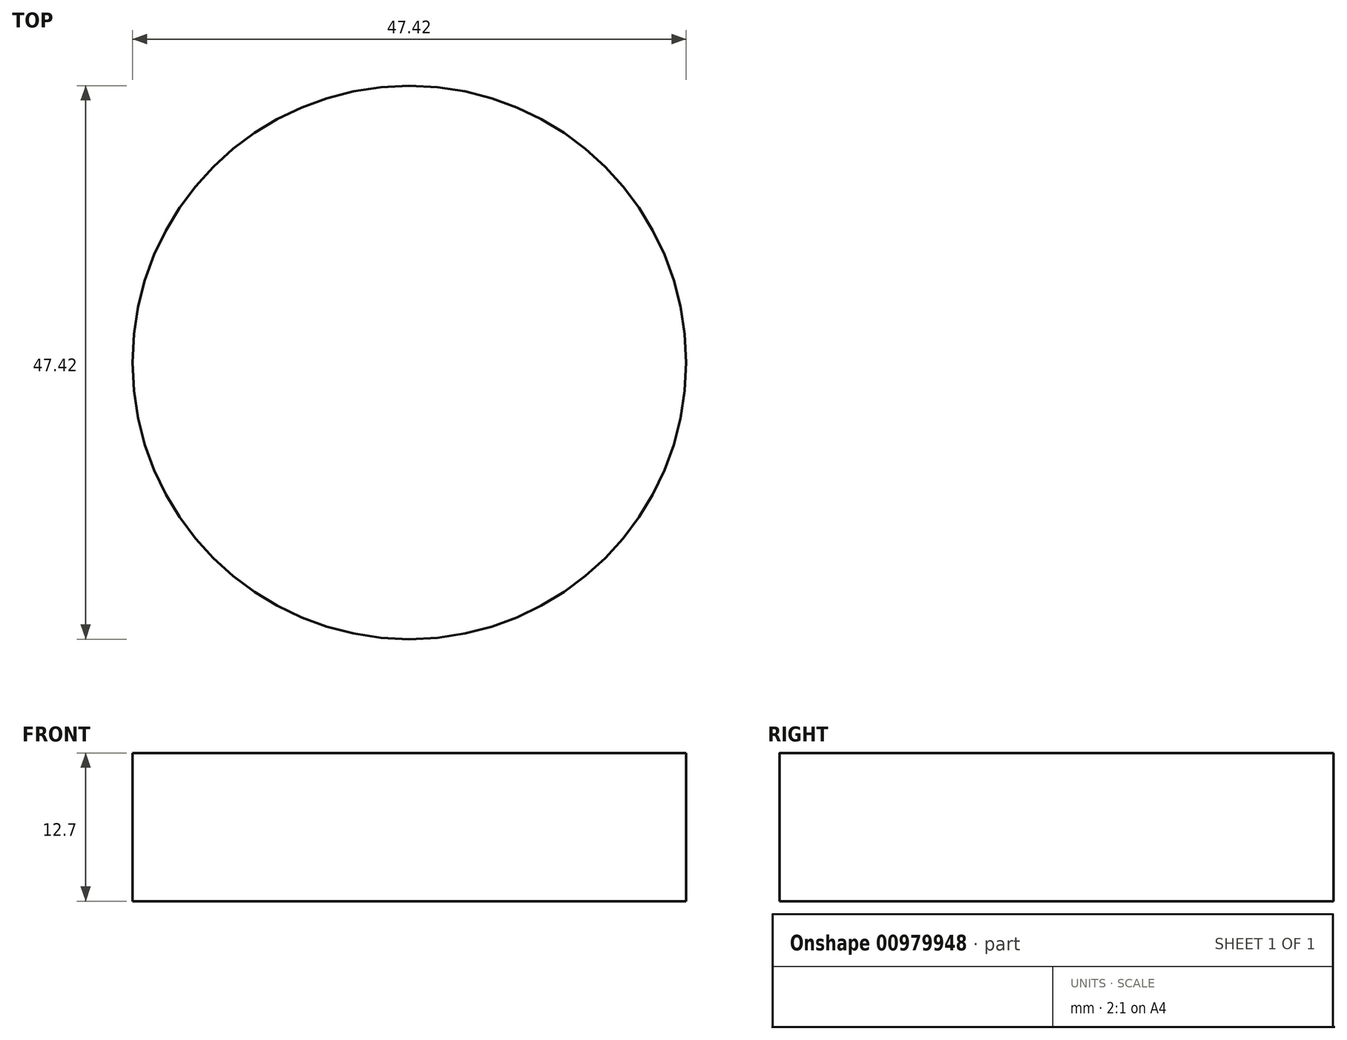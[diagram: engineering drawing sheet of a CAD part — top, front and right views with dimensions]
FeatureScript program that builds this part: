
annotation { "Feature Type Name" : "Feature", "Feature Type Description" : "" }
export const myFeature = defineFeature(function(context is Context, id is Id, definition is map)
    precondition{}
    {
        {
            var Q0;
            Q0=qCreatedBy(makeId("Top.planeOp"),FACE);
            var sketch = newSketch(context, id + "F0", { "sketchPlane" : qUnion([Q0])});
            skCircle(sketch, "E0", {"center": v(0, 0) * mm, "radius": 27.09 * mm, "construction": true});
            skCircle(sketch, "E1", {"center": v(0, 0) * mm, "radius": 25.4 * mm, "construction": true});
            skLineSegment(sketch, "E2", {"start": v(0, 0) * mm, "end": v(0, 43.65) * mm, "construction": true});
            skLineSegment(sketch, "E3", {"start": v(0, 0) * mm, "end": v(-2.28, 43.47) * mm, "construction": true});
            skCircle(sketch, "E4", {"center": v(0, 0) * mm, "radius": 23.71 * mm});
            skSolve(sketch);
        }
        {
            var Q0;
            {var subQ0=sQuery(id+"F0.wireOp",EDGE,"E4");var subQ1=makeQuery(id+"F0.imprint","INTERSECT",VERTEX,{"derivedFrom":[subQ0,sQuery(id+"F0.wireOp",EDGE,"tSjKOfbb-daJX-vA77-JAcX-qPdk99mpz8Vl")]});Q0=makeQuery(id+"F0.imprint","IMPRINT",FACE,{"disambiguationData":[TD([[makeQuery(id+"F0.imprint","IMPRINT",EDGE,{"disambiguationData":[TD([[subQ1,-1.0]])],"derivedFrom":subQ0}),1.0]])]});}
            var Q1;
            {var subQ0=sQuery(id+"F0.wireOp",EDGE,"tSjKOfbb-daJX-vA77-JAcX-qPdk99mpz8Vl");Q1=makeQuery(id+"F0.imprint","IMPRINT",FACE,{"disambiguationData":[TD([[makeQuery(id+"F0.imprint","IMPRINT",EDGE,{"derivedFrom":subQ0}),1.0]])]});}
            extrude(context, id + "F1", {"entities" : qUnion([Q0, Q1]), "depth" : 12.7 * mm, "offsetDistance" : 25.4 * mm});
        }
        {
            var Q0;
            Q0=makeQuery(id+"F1.opExtrude","SWEPT_BODY",BODY,{"disambiguationData":[OSD([sQuery(id+"F0.wireOp",EDGE,"E4"),sQuery(id+"F0.wireOp",EDGE,"tSjKOfbb-daJX-vA77-JAcX-qPdk99mpz8Vl"),sQuery(id+"F0.wireOp",EDGE,"ZkwQCzSm-2Mjk-RzL6-AbmB-f368mlHkzKaz"),sQuery(id+"F0.wireOp",EDGE,"2cc08034-d6be-4a9c-854b-d7df702918c30.MirrorCS"),sQuery(id+"F0.wireOp",EDGE,"a5fb16c4-e4b9-4578-ba91-38fe9ea5789b0.MirrorCS"),sQuery(id+"F0.wireOp",EDGE,"ctM98EgK-R19Y-fvTn-ngvH-sN4XsngqJa4U")])]});
            var Q1;
            Q1=makeQuery(id+"F1.opExtrude","SWEPT_FACE",FACE,{"disambiguationData":[OSD([sQuery(id+"F0.wireOp",EDGE,"E4")])]});
            circularPattern(context, id + "F2", {"entities" : qUnion([Q0]), "axis" : qUnion([Q1]), "angle" : 360 * degree, "instanceCount" : 30, "equalSpace" : true});
        }
        {
            var Q0;
            {var subQ0=sQuery(id+"F0.wireOp",EDGE,"E4");var subQ1=makeQuery(id+"F0.imprint","INTERSECT",VERTEX,{"derivedFrom":[subQ0,sQuery(id+"F0.wireOp",EDGE,"JFlq3OaX-p164-4u1S-Hzj9-ymQmPWCr5Qrh")]});Q0=makeQuery(id+"F0.imprint","IMPRINT",FACE,{"disambiguationData":[TD([[makeQuery(id+"F0.imprint","IMPRINT",EDGE,{"disambiguationData":[TD([[subQ1,-1.0]])],"derivedFrom":subQ0}),1.0]])]});}
            var Q1;
            Q1=makeQuery(id+"F0.imprint","IMPRINT",FACE,{"disambiguationData":[TD([[makeQuery(id+"F0.imprint","IMPRINT",EDGE,{"derivedFrom":sQuery(id+"F0.wireOp",EDGE,"NUCSSG6N-Tl5G-pkCQ-ays7-fCppW6AwSuHi")}),1.0]])]});
            extrude(context, id + "F3", {"entities" : qUnion([Q0, Q1]), "depth" : 12.7 * mm, "offsetDistance" : 25.4 * mm});
        }
        {
            var Q0;
            Q0=makeQuery(id+"F3.opExtrude","SWEPT_BODY",BODY,{"disambiguationData":[OSD([sQuery(id+"F0.wireOp",EDGE,"E4"),sQuery(id+"F0.wireOp",EDGE,"NUCSSG6N-Tl5G-pkCQ-ays7-fCppW6AwSuHi"),sQuery(id+"F0.wireOp",EDGE,"JFlq3OaX-p164-4u1S-Hzj9-ymQmPWCr5Qrh"),sQuery(id+"F0.wireOp",EDGE,"2f7721dc-f534-4744-a7ee-59b8e987721d0.MirrorCS"),sQuery(id+"F0.wireOp",EDGE,"5962244e-e064-48c4-8fdf-3d537b4d25f40.MirrorCS"),sQuery(id+"F0.wireOp",EDGE,"bcFN1io3-TrxV-2cOP-GvgK-YjUlUBRXKa2T")])]});
            var Q1;
            Q1=makeQuery(id+"F3.opExtrude","SWEPT_FACE",FACE,{"disambiguationData":[OSD([sQuery(id+"F0.wireOp",EDGE,"E4")])]});
            circularPattern(context, id + "F4", {"entities" : qUnion([Q0]), "axis" : qUnion([Q1]), "angle" : 360 * degree, "instanceCount" : 30, "equalSpace" : true});
        }
    });
